# Revit family: 3100.183.1  Roof Drain
name_source: partatom
category: Plumbing Fixtures
units: mm (PartAtom-declared; Revit-internal decimal feet)

## family parameters
Always vertical = Yes
Cut with Voids When Loaded = No
OmniClass Number = 23.45.00.00
OmniClass Title = Sanitary, Laundry, and Cleaning Equipment
Part Type = Normal
Room Calculation Point = No
Round Connector Dimension = Use Diameter
Shared = No
Work Plane-Based = No

## types (2) — shared parameters
CW Connection = No
Description = Roof Drain Side Exit 80mm Inlet x 80mm Outlet Small Flange
HW Connection = No
Manufacturer = Aquanight Industries Ltd
URL = www.aquaknight.co.nz
Vent Connection = Yes
Waste Connection = Yes
zero-valued in all types: Default Elevation

## per-type parameters (varying)
| type | Model | Overflow |
| 3100.183.1 80x80 Drain | 3100.183 | No |
| 3100.183.1 80x80 Overflow | 3100.183.1 | Yes |

## geometry (parser evidence)
native form markers: Sweep x4
no freeform markers — native parametric forms only
